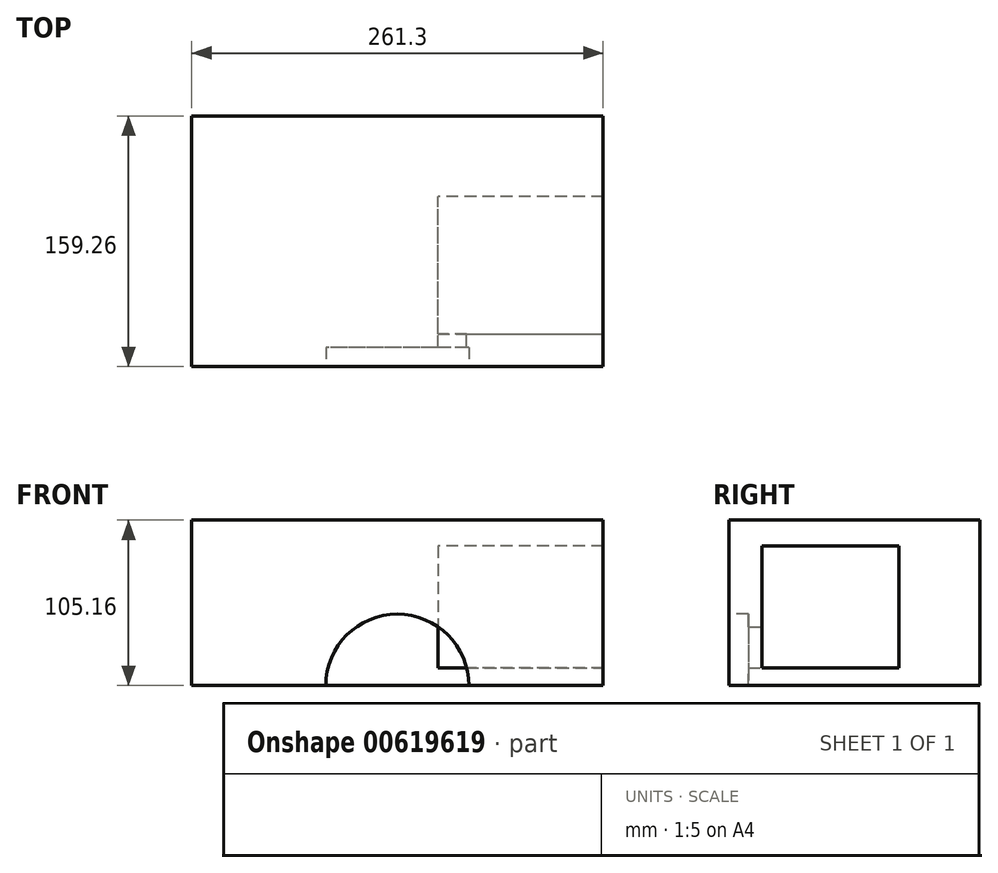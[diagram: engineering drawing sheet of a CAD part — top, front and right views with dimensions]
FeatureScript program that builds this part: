
annotation { "Feature Type Name" : "Feature", "Feature Type Description" : "" }
export const myFeature = defineFeature(function(context is Context, id is Id, definition is map)
    precondition{}
    {
        {
            var Q0;
            Q0=qCreatedBy(makeId("Top.planeOp"),FACE);
            var sketch = newSketch(context, id + "F0", { "sketchPlane" : qUnion([Q0])});
            skLineSegment(sketch, "E0.bottom", {"start": v(74.68, -68.46) * mm, "end": v(-186.62, -68.46) * mm});
            skLineSegment(sketch, "E0.top", {"start": v(74.68, 90.8) * mm, "end": v(-186.62, 90.8) * mm});
            skLineSegment(sketch, "E0.left", {"start": v(74.68, -68.46) * mm, "end": v(74.68, 90.8) * mm});
            skLineSegment(sketch, "E0.right", {"start": v(-186.62, -68.46) * mm, "end": v(-186.62, 90.8) * mm});
            skSolve(sketch);
        }
        {
            var Q0;
            Q0=makeQuery(id+"F0.imprint","IMPRINT",FACE,{"disambiguationData":[TD([[makeQuery(id+"F0.imprint","IMPRINT",EDGE,{"derivedFrom":sQuery(id+"F0.wireOp",EDGE,"E0.bottom")}),-1.0]])]});
            extrude(context, id + "F1", {"entities" : qUnion([Q0]), "depth" : 105.16 * mm, "offsetDistance" : 25.4 * mm});
        }
        {
            var Q0;
            Q0=makeQuery(id+"F1.opExtrude","SWEPT_FACE",FACE,{"disambiguationData":[OSD([sQuery(id+"F0.wireOp",EDGE,"E0.left")])]});
            var sketch = newSketch(context, id + "F2", { "sketchPlane" : qUnion([Q0])});
            skLineSegment(sketch, "E1.bottom", {"start": v(-47.65, 88.77) * mm, "end": v(72.32, 88.77) * mm});
            skLineSegment(sketch, "E1.top", {"start": v(-47.65, 11.34) * mm, "end": v(72.32, 11.34) * mm});
            skLineSegment(sketch, "E1.left", {"start": v(-47.65, 88.77) * mm, "end": v(-47.65, 11.34) * mm});
            skLineSegment(sketch, "E1.right", {"start": v(72.32, 88.77) * mm, "end": v(72.32, 11.34) * mm});
            skSolve(sketch);
        }
        {
            var Q0;
            Q0=makeQuery(id+"F2.imprint","IMPRINT",FACE,{"disambiguationData":[TD([[makeQuery(id+"F2.imprint","IMPRINT",EDGE,{"derivedFrom":sQuery(id+"F2.wireOp",EDGE,"E1.bottom")}),-1.0]])]});
            extrude(context, id + "F3", {"entities" : qUnion([Q0]), "operationType" : NewBodyOperationType.REMOVE, "oppositeDirection" : true, "depth" : 104.9 * mm, "offsetDistance" : 25.4 * mm});
        }
        {
            var Q0;
            Q0=makeQuery(id+"F1.opExtrude","SWEPT_FACE",FACE,{"disambiguationData":[OSD([sQuery(id+"F0.wireOp",EDGE,"E0.bottom")])]});
            var sketch = newSketch(context, id + "F4", { "sketchPlane" : qUnion([Q0])});
            skCircle(sketch, "E2", {"center": v(-55.97, 0) * mm, "radius": 45.44 * mm});
            skSolve(sketch);
        }
        {
            var Q0;
            {var subQ0=sQuery(id+"F4.wireOp",EDGE,"E2");var subQ1=makeQuery(id+"F1.opExtrude","CAP_EDGE",EDGE,{"disambiguationData":[OSD([sQuery(id+"F0.wireOp",EDGE,"E0.bottom")])],"isStart":true});var subQ2=makeQuery(id+"F4.imprint","INTERSECT",VERTEX,{"disambiguationData":[OD(0.0)],"derivedFrom":[subQ1,subQ0]});Q0=makeQuery(id+"F4.imprint","IMPRINT",FACE,{"disambiguationData":[TD([[makeQuery(id+"F4.imprint","IMPRINT",EDGE,{"disambiguationData":[TD([[subQ2,-1.0]])],"derivedFrom":subQ0}),1.0]])]});}
            extrude(context, id + "F5", {"entities" : qUnion([Q0]), "operationType" : NewBodyOperationType.REMOVE, "oppositeDirection" : true, "depth" : 63.5 * mm, "offsetDistance" : 25.4 * mm});
        }
        {
            var Q0;
            Q0=makeQuery(id+"F1.opExtrude","SWEPT_FACE",FACE,{"disambiguationData":[OSD([sQuery(id+"F0.wireOp",EDGE,"E0.top")])]});
            var sketch = newSketch(context, id + "F6", { "sketchPlane" : qUnion([Q0])});
            skCircle(sketch, "E3", {"center": v(52.66, 0) * mm, "radius": 48.28 * mm});
            skSolve(sketch);
        }
        {
            var Q0;
            {var subQ0=sQuery(id+"F6.wireOp",EDGE,"E3");var subQ1=makeQuery(id+"F1.opExtrude","CAP_EDGE",EDGE,{"disambiguationData":[OSD([sQuery(id+"F0.wireOp",EDGE,"E0.top")])],"isStart":true});var subQ2=makeQuery(id+"F6.imprint","INTERSECT",VERTEX,{"disambiguationData":[OD(0.0)],"derivedFrom":[subQ1,subQ0]});Q0=makeQuery(id+"F6.imprint","IMPRINT",FACE,{"disambiguationData":[TD([[makeQuery(id+"F6.imprint","IMPRINT",EDGE,{"disambiguationData":[TD([[subQ2,1.0]])],"derivedFrom":subQ0}),1.0]])]});}
            var Q1;
            Q1=makeQuery(id+"F1.opExtrude","SWEPT_FACE",FACE,{"disambiguationData":[OSD([sQuery(id+"F0.wireOp",EDGE,"E0.top")])]});
            var Q2;
            Q2=makeQuery(id+"F5.boolean.opBoolean","COPY",FACE,{"derivedFrom":makeQuery(id+"F5.opExtrude","CAP_FACE",FACE,{"disambiguationData":[OSD([sQuery(id+"F0.wireOp",EDGE,"E0.bottom"),sQuery(id+"F4.wireOp",EDGE,"E2")])],"isStart":false})});
            extrude(context, id + "F7", {"entities" : qUnion([Q0, Q1, Q2]), "operationType" : NewBodyOperationType.ADD, "oppositeDirection" : true, "depth" : 51.3 * mm, "offsetDistance" : 25.4 * mm});
        }
    });
